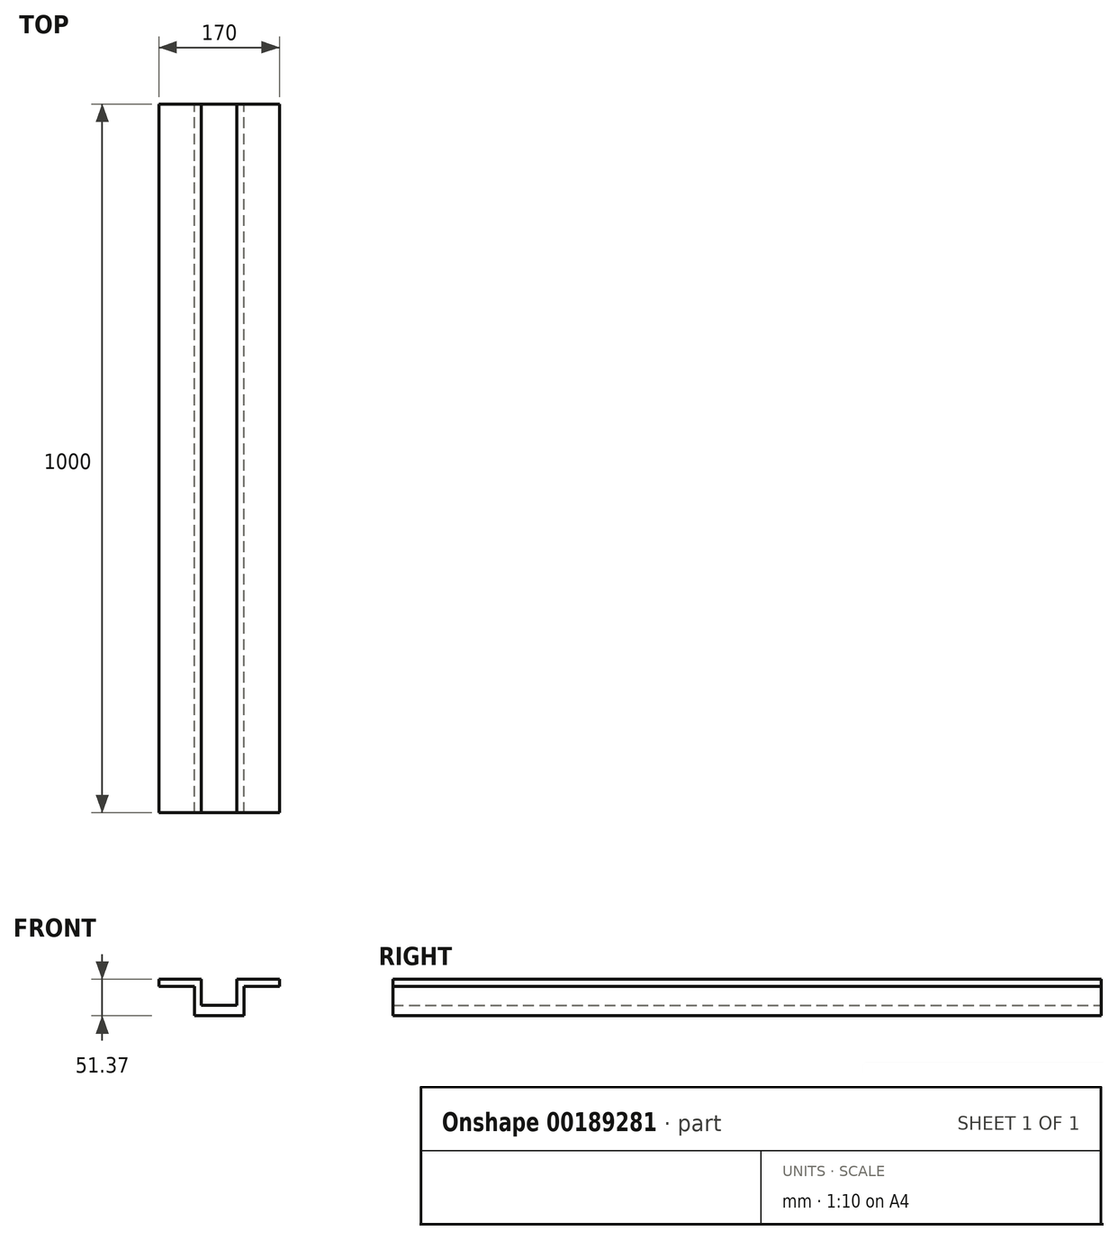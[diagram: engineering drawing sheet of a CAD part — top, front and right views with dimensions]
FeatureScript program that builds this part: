
annotation { "Feature Type Name" : "Feature", "Feature Type Description" : "" }
export const myFeature = defineFeature(function(context is Context, id is Id, definition is map)
    precondition{}
    {
        {
            var Q0;
            Q0=qCreatedBy(makeId("Front.planeOp"),FACE);
            var sketch = newSketch(context, id + "F0", { "sketchPlane" : qUnion([Q0])});
            skLineSegment(sketch, "E0.bottom", {"start": v(-85, 43.87) * mm, "end": v(-35, 43.87) * mm});
            skLineSegment(sketch, "E0.top", {"start": v(-85, 33.87) * mm, "end": v(-35, 33.87) * mm});
            skLineSegment(sketch, "E0.left", {"start": v(-85, 43.87) * mm, "end": v(-85, 33.87) * mm});
            skLineSegment(sketch, "E0.right", {"start": v(-35, 43.87) * mm, "end": v(-35, 33.87) * mm});
            skPoint(sketch, "E0.middle", {"position": v(-60, 38.87) * mm});
            skLineSegment(sketch, "E1.MirrorCS", {"start": v(85, 43.87) * mm, "end": v(35, 43.87) * mm});
            skLineSegment(sketch, "E2.MirrorCS", {"start": v(35, 43.87) * mm, "end": v(35, 33.87) * mm});
            skLineSegment(sketch, "E3.MirrorCS", {"start": v(85, 33.87) * mm, "end": v(35, 33.87) * mm});
            skLineSegment(sketch, "E4.MirrorCS", {"start": v(85, 43.87) * mm, "end": v(85, 33.87) * mm});
            skLineSegment(sketch, "E5.bottom", {"start": v(-25, 7.5) * mm, "end": v(25, 7.5) * mm});
            skLineSegment(sketch, "E5.top", {"start": v(-25, -7.5) * mm, "end": v(25, -7.5) * mm});
            skLineSegment(sketch, "E5.left", {"start": v(-25, 7.5) * mm, "end": v(-25, -7.5) * mm});
            skLineSegment(sketch, "E5.right", {"start": v(25, 7.5) * mm, "end": v(25, -7.5) * mm});
            skPoint(sketch, "E5.middle", {"position": v(0, 0) * mm});
            skLineSegment(sketch, "E6.bottom", {"start": v(-35, 43.87) * mm, "end": v(-25, 43.87) * mm});
            skLineSegment(sketch, "E6.top", {"start": v(-35, -7.5) * mm, "end": v(-25, -7.5) * mm});
            skLineSegment(sketch, "E6.left", {"start": v(-35, 43.87) * mm, "end": v(-35, -7.5) * mm});
            skLineSegment(sketch, "E6.right", {"start": v(-25, 43.87) * mm, "end": v(-25, -7.5) * mm});
            skLineSegment(sketch, "E7.MirrorCS", {"start": v(25, 43.87) * mm, "end": v(25, -7.5) * mm});
            skLineSegment(sketch, "E8.MirrorCS", {"start": v(35, 43.87) * mm, "end": v(35, -7.5) * mm});
            skLineSegment(sketch, "E9.MirrorCS", {"start": v(35, 43.87) * mm, "end": v(25, 43.87) * mm});
            skLineSegment(sketch, "E10.MirrorCS", {"start": v(35, -7.5) * mm, "end": v(25, -7.5) * mm});
            skSolve(sketch);
        }
        {
            var Q0;
            {var subQ0=sQuery(id+"F0.wireOp",EDGE,"E0.bottom");Q0=makeQuery(id+"F0.imprint","IMPRINT",FACE,{"disambiguationData":[TD([[makeQuery(id+"F0.imprint","IMPRINT",EDGE,{"derivedFrom":subQ0}),-1.0]])]});}
            var Q1;
            {var subQ3=sQuery(id+"F0.wireOp",EDGE,"E6.bottom");Q1=makeQuery(id+"F0.imprint","IMPRINT",FACE,{"disambiguationData":[TD([[makeQuery(id+"F0.imprint","IMPRINT",EDGE,{"derivedFrom":subQ3}),-1.0]])]});}
            var Q2;
            {var subQ0=sQuery(id+"F0.wireOp",EDGE,"E5.bottom");Q2=makeQuery(id+"F0.imprint","IMPRINT",FACE,{"disambiguationData":[TD([[makeQuery(id+"F0.imprint","IMPRINT",EDGE,{"derivedFrom":subQ0}),-1.0]])]});}
            var Q3;
            {var subQ3=sQuery(id+"F0.wireOp",EDGE,"E9.MirrorCS");Q3=makeQuery(id+"F0.imprint","IMPRINT",FACE,{"disambiguationData":[TD([[makeQuery(id+"F0.imprint","IMPRINT",EDGE,{"derivedFrom":subQ3}),1.0]])]});}
            var Q4;
            {var subQ0=sQuery(id+"F0.wireOp",EDGE,"E1.MirrorCS");Q4=makeQuery(id+"F0.imprint","IMPRINT",FACE,{"disambiguationData":[TD([[makeQuery(id+"F0.imprint","IMPRINT",EDGE,{"derivedFrom":subQ0}),1.0]])]});}
            extrude(context, id + "F1", {"entities" : qUnion([Q0, Q1, Q2, Q3, Q4]), "depth" : 1000 * mm});
        }
    });
